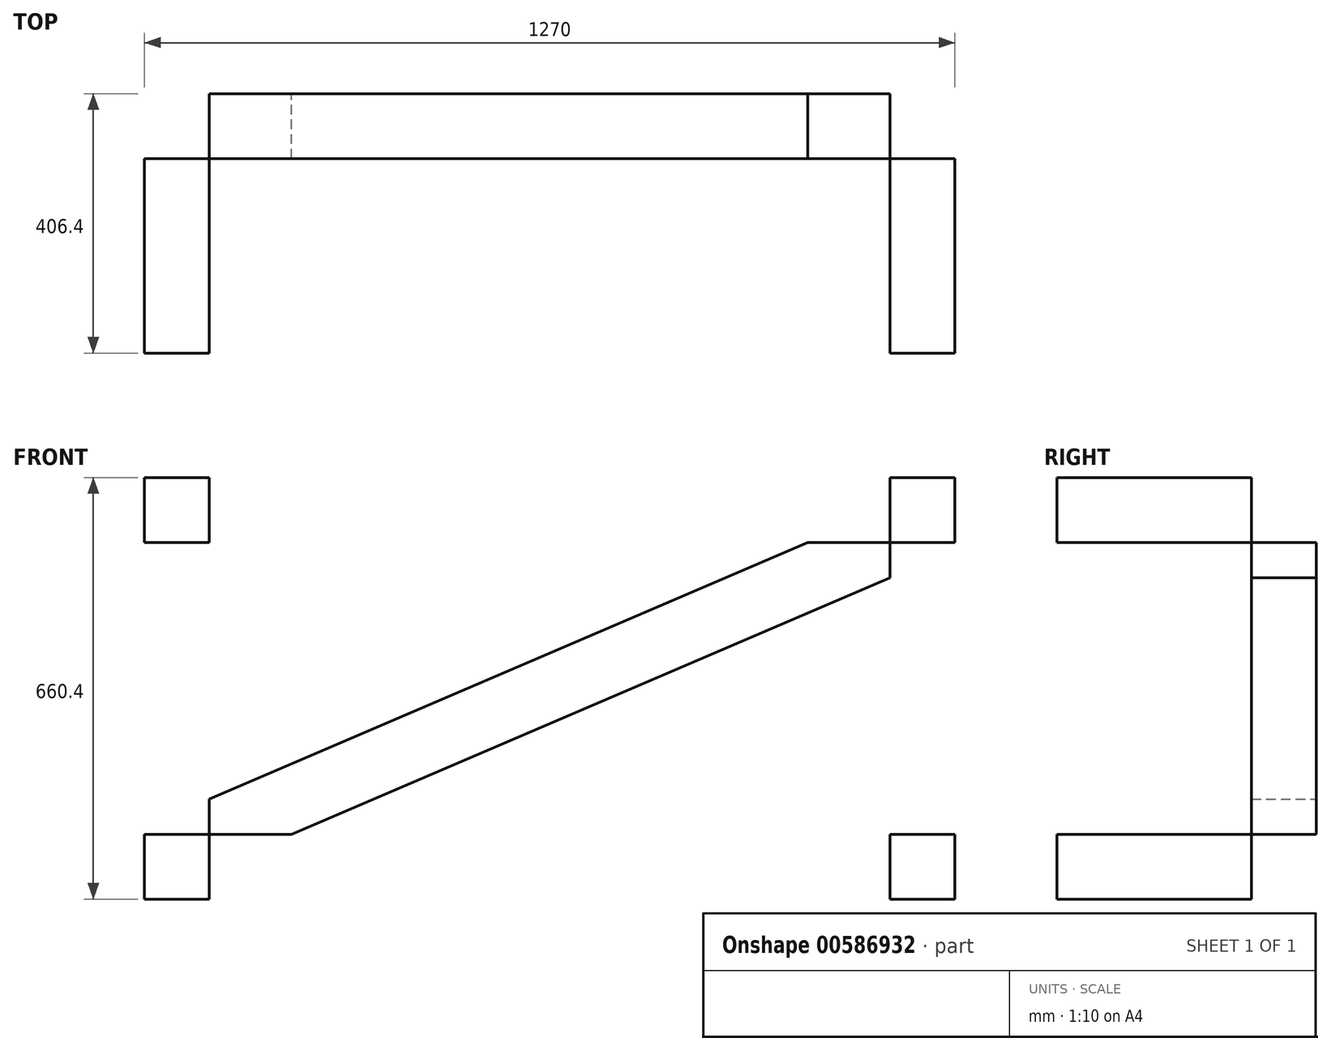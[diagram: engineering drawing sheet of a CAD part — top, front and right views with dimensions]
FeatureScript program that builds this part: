
annotation { "Feature Type Name" : "Feature", "Feature Type Description" : "" }
export const myFeature = defineFeature(function(context is Context, id is Id, definition is map)
    precondition{}
    {
        {
            var Q0;
            Q0=qCreatedBy(makeId("Front.planeOp"),FACE);
            var sketch = newSketch(context, id + "F0", { "sketchPlane" : qUnion([Q0])});
            skLineSegment(sketch, "E0.bottom", {"start": v(533.4, -228.6) * mm, "end": v(-533.4, -228.6) * mm});
            skLineSegment(sketch, "E0.top", {"start": v(533.4, 228.6) * mm, "end": v(-533.4, 228.6) * mm});
            skLineSegment(sketch, "E0.left", {"start": v(533.4, -228.6) * mm, "end": v(533.4, 228.6) * mm});
            skLineSegment(sketch, "E0.right", {"start": v(-533.4, -228.6) * mm, "end": v(-533.4, 228.6) * mm});
            skPoint(sketch, "E0.middle", {"position": v(0, 0) * mm});
            skLineSegment(sketch, "E1.bottom", {"start": v(635, -330.2) * mm, "end": v(-635, -330.2) * mm});
            skLineSegment(sketch, "E1.top", {"start": v(635, 330.2) * mm, "end": v(-635, 330.2) * mm});
            skLineSegment(sketch, "E1.left", {"start": v(635, -330.2) * mm, "end": v(635, 330.2) * mm});
            skLineSegment(sketch, "E1.right", {"start": v(-635, -330.2) * mm, "end": v(-635, 330.2) * mm});
            skLineSegment(sketch, "E2", {"start": v(404.44, 228.6) * mm, "end": v(-533.4, -173.33) * mm});
            skLineSegment(sketch, "E3", {"start": v(533.4, 173.33) * mm, "end": v(-404.44, -228.6) * mm});
            skSolve(sketch);
        }
        {
            var Q0;
            Q0=makeQuery(id+"F0.imprint","IMPRINT",FACE,{"disambiguationData":[TD([[makeQuery(id+"F0.imprint","IMPRINT",EDGE,{"derivedFrom":sQuery(id+"F0.wireOp",EDGE,"E1.bottom")}),-1.0]])]});
            var Q1;
            {var subQ4=sQuery(id+"F0.wireOp",EDGE,"E2");Q1=makeQuery(id+"F0.imprint","IMPRINT",FACE,{"disambiguationData":[TD([[makeQuery(id+"F0.imprint","IMPRINT",EDGE,{"derivedFrom":subQ4}),1.0]])]});}
            extrude(context, id + "F1", {"entities" : qUnion([Q0, Q1]), "depth" : 101.6 * mm, "offsetDistance" : 25.4 * mm});
        }
        {
            var Q0;
            Q0=makeQuery(id+"F1.opExtrude","CAP_FACE",FACE,{"disambiguationData":[OSD([sQuery(id+"F0.wireOp",EDGE,"E0.bottom"),sQuery(id+"F0.wireOp",EDGE,"E0.top"),sQuery(id+"F0.wireOp",EDGE,"E0.left"),sQuery(id+"F0.wireOp",EDGE,"E0.right"),sQuery(id+"F0.wireOp",EDGE,"E1.bottom"),sQuery(id+"F0.wireOp",EDGE,"E1.top"),sQuery(id+"F0.wireOp",EDGE,"E1.left"),sQuery(id+"F0.wireOp",EDGE,"E1.right"),sQuery(id+"F0.wireOp",EDGE,"E2"),sQuery(id+"F0.wireOp",EDGE,"E3")])],"isStart":false});
            var sketch = newSketch(context, id + "F2", { "sketchPlane" : qUnion([Q0])});
            skLineSegment(sketch, "E4.0", {"start": v(-533.4, 330.2) * mm, "end": v(-635, 330.2) * mm});
            skLineSegment(sketch, "E5.0", {"start": v(-635, 228.6) * mm, "end": v(-635, 330.2) * mm});
            skLineSegment(sketch, "E6", {"start": v(-533.4, 228.6) * mm, "end": v(-533.4, 330.2) * mm});
            skLineSegment(sketch, "E7", {"start": v(-533.4, 228.6) * mm, "end": v(-635, 228.6) * mm});
            skPoint(sketch, "E8.orphan", {"position": v(-635, -330.2) * mm});
            skPoint(sketch, "E9.orphan", {"position": v(635, 330.2) * mm});
            skPoint(sketch, "E10.0.start.orphan", {"position": v(404.44, 228.6) * mm});
            skPoint(sketch, "E11.0.start.orphan", {"position": v(-533.4, -173.33) * mm});
            skSolve(sketch);
        }
        {
            var Q0;
            Q0 = qSketchRegion(id + "F2", true);
            extrude(context, id + "F3", {"entities" : qUnion([Q0]), "operationType" : NewBodyOperationType.ADD, "depth" : 304.8 * mm, "offsetDistance" : 25.4 * mm});
        }
        {
            var Q0;
            Q0=makeQuery(id+"F1.opExtrude","CAP_FACE",FACE,{"disambiguationData":[OSD([sQuery(id+"F0.wireOp",EDGE,"E0.bottom"),sQuery(id+"F0.wireOp",EDGE,"E0.top"),sQuery(id+"F0.wireOp",EDGE,"E0.left"),sQuery(id+"F0.wireOp",EDGE,"E0.right"),sQuery(id+"F0.wireOp",EDGE,"E1.bottom"),sQuery(id+"F0.wireOp",EDGE,"E1.top"),sQuery(id+"F0.wireOp",EDGE,"E1.left"),sQuery(id+"F0.wireOp",EDGE,"E1.right"),sQuery(id+"F0.wireOp",EDGE,"E2"),sQuery(id+"F0.wireOp",EDGE,"E3")])],"isStart":false});
            var sketch = newSketch(context, id + "F4", { "sketchPlane" : qUnion([Q0])});
            skLineSegment(sketch, "E12.bottom", {"start": v(-635, -330.2) * mm, "end": v(-533.4, -330.2) * mm});
            skLineSegment(sketch, "E12.top", {"start": v(-635, -228.6) * mm, "end": v(-533.4, -228.6) * mm});
            skLineSegment(sketch, "E12.left", {"start": v(-635, -330.2) * mm, "end": v(-635, -228.6) * mm});
            skLineSegment(sketch, "E12.right", {"start": v(-533.4, -330.2) * mm, "end": v(-533.4, -228.6) * mm});
            skSolve(sketch);
        }
        {
            var Q0;
            Q0 = qSketchRegion(id + "F4", true);
            extrude(context, id + "F5", {"entities" : qUnion([Q0]), "operationType" : NewBodyOperationType.ADD, "depth" : 304.8 * mm, "offsetDistance" : 25.4 * mm});
        }
        {
            var Q0;
            Q0 = qSketchRegion(id + "F4", true);
            extrude(context, id + "F6", {"entities" : qUnion([Q0]), "operationType" : NewBodyOperationType.ADD, "depth" : 304.8 * mm, "offsetDistance" : 25.4 * mm});
        }
        {
            var Q0;
            Q0=makeQuery(id+"F1.opExtrude","CAP_FACE",FACE,{"disambiguationData":[OSD([sQuery(id+"F0.wireOp",EDGE,"E0.bottom"),sQuery(id+"F0.wireOp",EDGE,"E0.top"),sQuery(id+"F0.wireOp",EDGE,"E0.left"),sQuery(id+"F0.wireOp",EDGE,"E0.right"),sQuery(id+"F0.wireOp",EDGE,"E1.bottom"),sQuery(id+"F0.wireOp",EDGE,"E1.top"),sQuery(id+"F0.wireOp",EDGE,"E1.left"),sQuery(id+"F0.wireOp",EDGE,"E1.right"),sQuery(id+"F0.wireOp",EDGE,"E2"),sQuery(id+"F0.wireOp",EDGE,"E3")])],"isStart":false});
            var sketch = newSketch(context, id + "F7", { "sketchPlane" : qUnion([Q0])});
            skLineSegment(sketch, "E13.bottom", {"start": v(635, -330.2) * mm, "end": v(533.4, -330.2) * mm});
            skLineSegment(sketch, "E13.top", {"start": v(635, -228.6) * mm, "end": v(533.4, -228.6) * mm});
            skLineSegment(sketch, "E13.left", {"start": v(635, -330.2) * mm, "end": v(635, -228.6) * mm});
            skLineSegment(sketch, "E13.right", {"start": v(533.4, -330.2) * mm, "end": v(533.4, -228.6) * mm});
            skSolve(sketch);
        }
        {
            var Q0;
            Q0=makeQuery(id+"F1.opExtrude","CAP_FACE",FACE,{"disambiguationData":[OSD([sQuery(id+"F0.wireOp",EDGE,"E0.bottom"),sQuery(id+"F0.wireOp",EDGE,"E0.top"),sQuery(id+"F0.wireOp",EDGE,"E0.left"),sQuery(id+"F0.wireOp",EDGE,"E0.right"),sQuery(id+"F0.wireOp",EDGE,"E1.bottom"),sQuery(id+"F0.wireOp",EDGE,"E1.top"),sQuery(id+"F0.wireOp",EDGE,"E1.left"),sQuery(id+"F0.wireOp",EDGE,"E1.right"),sQuery(id+"F0.wireOp",EDGE,"E2"),sQuery(id+"F0.wireOp",EDGE,"E3")])],"isStart":false});
            var sketch = newSketch(context, id + "F8", { "sketchPlane" : qUnion([Q0])});
            skLineSegment(sketch, "E14.bottom", {"start": v(635, 330.2) * mm, "end": v(533.4, 330.2) * mm});
            skLineSegment(sketch, "E14.top", {"start": v(635, 228.6) * mm, "end": v(533.4, 228.6) * mm});
            skLineSegment(sketch, "E14.left", {"start": v(635, 330.2) * mm, "end": v(635, 228.6) * mm});
            skLineSegment(sketch, "E14.right", {"start": v(533.4, 330.2) * mm, "end": v(533.4, 228.6) * mm});
            skSolve(sketch);
        }
        {
            var Q0;
            Q0 = qSketchRegion(id + "F8", true);
            extrude(context, id + "F9", {"entities" : qUnion([Q0]), "operationType" : NewBodyOperationType.ADD, "depth" : 304.8 * mm, "offsetDistance" : 25.4 * mm});
        }
        {
            var Q0;
            Q0=makeQuery(id+"F7.imprint","IMPRINT",FACE,{"disambiguationData":[TD([[makeQuery(id+"F7.imprint","IMPRINT",EDGE,{"derivedFrom":sQuery(id+"F7.wireOp",EDGE,"E13.bottom")}),-1.0]])]});
            extrude(context, id + "F10", {"entities" : qUnion([Q0]), "operationType" : NewBodyOperationType.ADD, "depth" : 304.8 * mm, "offsetDistance" : 25.4 * mm});
        }
    });
